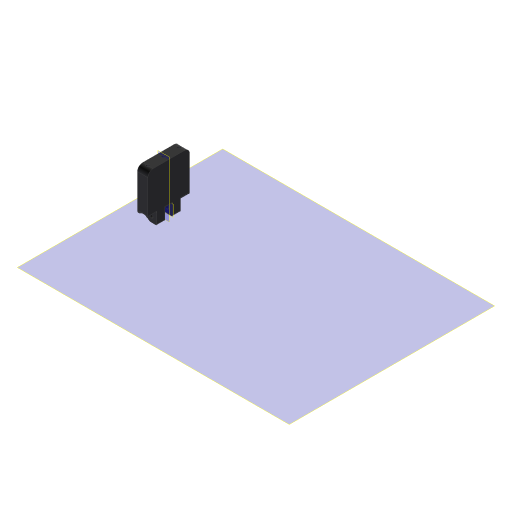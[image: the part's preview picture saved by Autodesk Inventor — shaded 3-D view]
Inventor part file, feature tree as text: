
AUTODESK INVENTOR PART (.ipt)
format: ipt  version: 2024.2 (Build 282272000, 272)  size: 205,312 bytes
history: native  units: mm
features: extrude x4, sketch x4, reference x4, plane x3, fillet x3, other x3, projected_geometry x2, mirror x1
ambient origin geometry x8: Origin, YZ Plane, XZ Plane, XY Plane, X Axis, Y Axis, Z Axis, Center Point
bodies: Volumenkörper1 (feature_tree)
feature tree (24):
  plane  "Arbeitsebene1"
  extrude  "Extrusion1"  Depth=10.0mm
  fillet  "Rundung1"  Radius=50.0mm
  extrude  "Extrusion2"  Depth=0.5mm
  plane  "Arbeitsebene2"
  extrude  "Extrusion3"  Depth=7.8mm TaperAngle=0.0deg
  plane  "Arbeitsebene3"
  extrude  "Extrusion4"  Depth=10.0mm TaperAngle=0.0deg
  fillet  "Fillet4"  Radius=1.0mm
  mirror  "Spiegeln1"
  fillet  "Rundung3"  [1 undecoded]
  sketch  "Skizze1"  dims[d0=10.0mm d1=40.0mm d2=50.0mm d3=0.0mm]
  reference  "Referenz1"
  sketch  "Skizze2"  dims[d4=5.0mm d5=0.5mm]
  reference  "Referenz2"
  reference  "Referenz3"
  projected_geometry  "Projizierte Kontur1"
  sketch  "Skizze3"  dims[d6=40.0mm d7=0.0mm d8=7.8mm d9=0.0mm]
  reference  "Referenz4"
  projected_geometry  "Projizierte Kontur2"
  sketch  "Sketch5"  dims[d11=2.0mm d12=10.0mm d13=0.0mm d14=1.0mm]
  other  "Assembly_Planktoscope_Uc2version_wormdrive_V3.iam"
  other  "60_Planktoscope_MicroscopeHolder_Bottom_v0:1"
  other  "60_Planktoscope_Illuminationsource:1"
note: 1 required parameter value undecoded (feature->parameter linkage not recoverable at this tier; creation-order binding heuristic only, values carry confidence <= 0.55)
